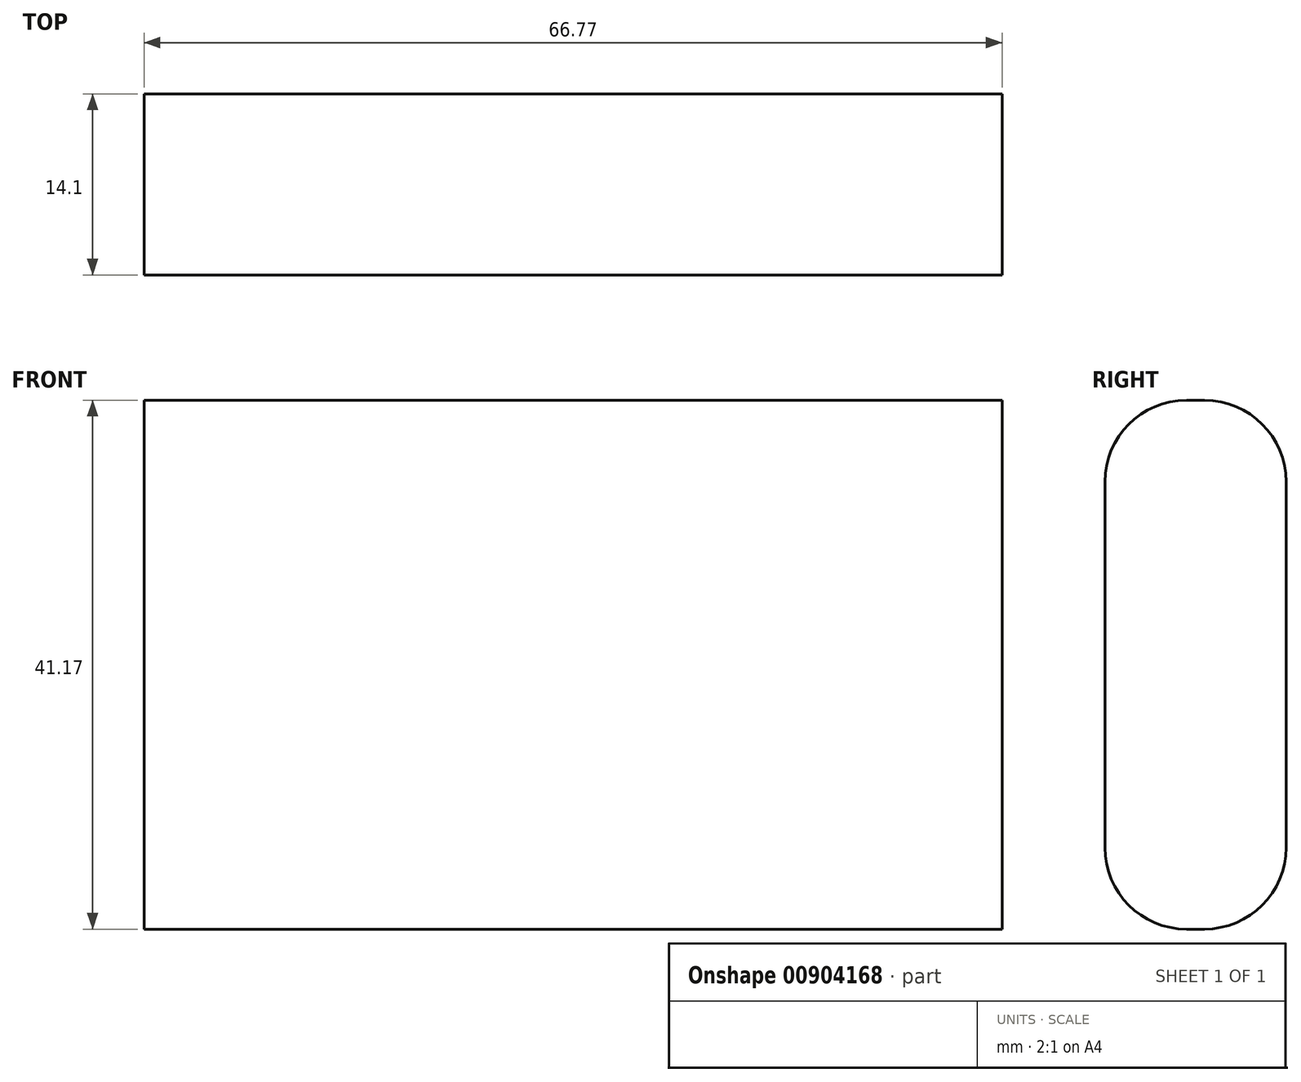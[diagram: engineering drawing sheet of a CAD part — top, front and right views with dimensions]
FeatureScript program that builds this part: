
annotation { "Feature Type Name" : "Feature", "Feature Type Description" : "" }
export const myFeature = defineFeature(function(context is Context, id is Id, definition is map)
    precondition{}
    {
        {
            var Q0;
            Q0=qCreatedBy(makeId("Front.planeOp"),FACE);
            var sketch = newSketch(context, id + "F0", { "sketchPlane" : qUnion([Q0])});
            skLineSegment(sketch, "E0.bottom", {"start": v(-6.37, 16.4) * mm, "end": v(60.4, 16.4) * mm});
            skLineSegment(sketch, "E0.top", {"start": v(-6.37, -24.77) * mm, "end": v(60.4, -24.77) * mm});
            skLineSegment(sketch, "E0.left", {"start": v(-6.37, 16.4) * mm, "end": v(-6.37, -24.77) * mm});
            skLineSegment(sketch, "E0.right", {"start": v(60.4, 16.4) * mm, "end": v(60.4, -24.77) * mm});
            skSolve(sketch);
        }
        {
            var Q0;
            Q0=makeQuery(id+"F0.imprint","IMPRINT",FACE,{"disambiguationData":[TD([[makeQuery(id+"F0.imprint","IMPRINT",EDGE,{"derivedFrom":sQuery(id+"F0.wireOp",EDGE,"E0.bottom")}),-1.0]])]});
            extrude(context, id + "F1", {"entities" : qUnion([Q0]), "depth" : 14.1 * mm, "offsetDistance" : 25.4 * mm});
        }
        {
            var Q0;
            Q0=makeQuery(id+"F1.opExtrude","CAP_EDGE",EDGE,{"disambiguationData":[OSD([sQuery(id+"F0.wireOp",EDGE,"E0.top")])],"isStart":false});
            var Q1;
            Q1=makeQuery(id+"F1.opExtrude","CAP_EDGE",EDGE,{"disambiguationData":[OSD([sQuery(id+"F0.wireOp",EDGE,"E0.top")])],"isStart":true});
            var Q2;
            Q2=makeQuery(id+"F1.opExtrude","CAP_EDGE",EDGE,{"disambiguationData":[OSD([sQuery(id+"F0.wireOp",EDGE,"E0.bottom")])],"isStart":false});
            var Q3;
            Q3=makeQuery(id+"F1.opExtrude","CAP_EDGE",EDGE,{"disambiguationData":[OSD([sQuery(id+"F0.wireOp",EDGE,"E0.bottom")])],"isStart":true});
            fillet(context, id + "F2", {"entities" : qUnion([Q0, Q1, Q2, Q3]), "radius" : 6.35 * mm, "tangentPropagation" : true, "allowEdgeOverflow" : false});
        }
    });
